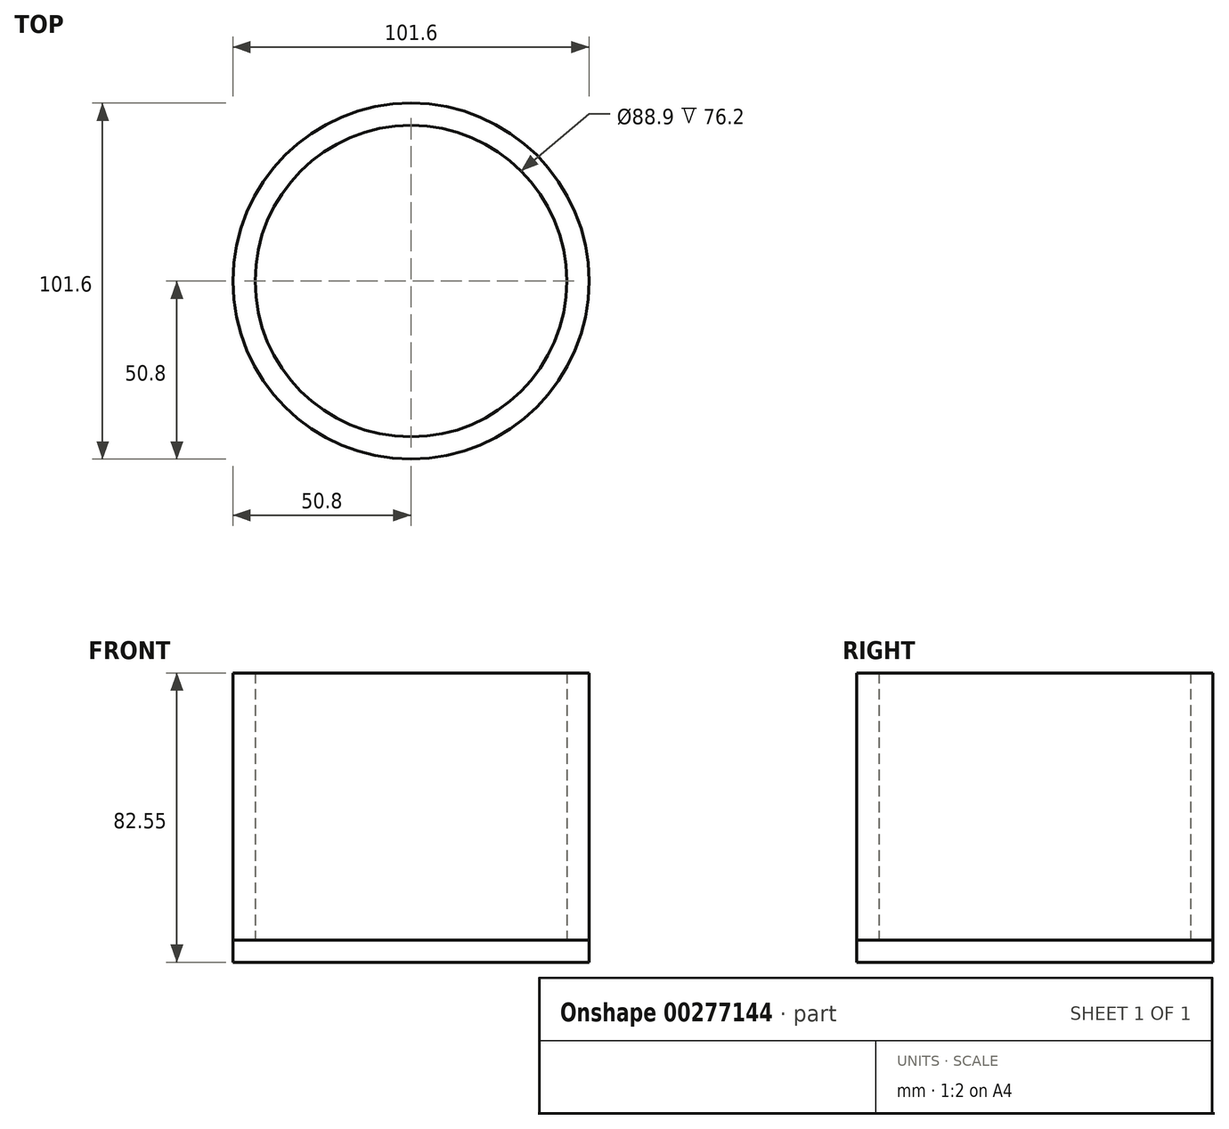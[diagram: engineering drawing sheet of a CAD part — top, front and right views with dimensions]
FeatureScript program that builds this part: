
annotation { "Feature Type Name" : "Feature", "Feature Type Description" : "" }
export const myFeature = defineFeature(function(context is Context, id is Id, definition is map)
    precondition{}
    {
        {
            var Q0;
            Q0=qCreatedBy(makeId("Top.planeOp"),FACE);
            var sketch = newSketch(context, id + "F0", { "sketchPlane" : qUnion([Q0])});
            skCircle(sketch, "E0", {"center": v(0, 0) * mm, "radius": 50.8 * mm});
            skCircle(sketch, "E1", {"center": v(0, 0) * mm, "radius": 44.45 * mm});
            skSolve(sketch);
        }
        {
            var Q0;
            Q0=makeQuery(id+"F0.imprint","IMPRINT",FACE,{"disambiguationData":[TD([[makeQuery(id+"F0.imprint","IMPRINT",EDGE,{"derivedFrom":sQuery(id+"F0.wireOp",EDGE,"E0")}),1.0]])]});
            extrude(context, id + "F1", {"entities" : qUnion([Q0]), "depth" : 76.2 * mm});
        }
        {
            var Q0;
            Q0=qCreatedBy(makeId("Top.planeOp"),FACE);
            var sketch = newSketch(context, id + "F2", { "sketchPlane" : qUnion([Q0])});
            skCircle(sketch, "E2", {"center": v(0, 0) * mm, "radius": 50.8 * mm});
            skSolve(sketch);
        }
        {
            var Q0;
            Q0=makeQuery(id+"F2.imprint","IMPRINT",FACE,{"disambiguationData":[TD([[makeQuery(id+"F2.imprint","IMPRINT",EDGE,{"derivedFrom":sQuery(id+"F2.wireOp",EDGE,"E2")}),1.0]])]});
            extrude(context, id + "F3", {"entities" : qUnion([Q0]), "oppositeDirection" : true, "depth" : 6.35 * mm});
        }
    });
